# Revit family: IVLB_L4U_GM_Track 3Phase - NORDIC XTS
name_source: partatom
category: Lighting Fixtures
units: mm (PartAtom-declared; Revit-internal decimal feet)

## family parameters
Always vertical = No
Cut with Voids When Loaded = No
Light Source = No
Part Type = Normal
Room Calculation Point = No
Round Connector Dimension = Use Diameter
Shared = No
Work Plane-Based = No

## types (4) — shared parameters
Apparent Load = 0 VA
Assembly Code = 63.00
IfcExportAs = IfcLightFixtureType
IfcExportType = POINTSOURCE
Manufacturer = Light4u
URL = www.ivlibrary.com
⌂ Powered by IVLibrary = www.ivlibrary.com

## per-type parameters (varying)
| type | Length |
| NORDIC XTS 4100 | 4100 mm  [stored 13.4514 ft] |
| NORDIC XTS 4200 | 4200 mm |
| NORDIC XTS 4300 | 4300 mm |
| NORDIC XTS 4400 | 4400 mm |

note: column(s) folded — value = type name in every type: Description, Model

note: [stored X ft] marks values corroborated as IEEE doubles in the binary element streams (Revit-internal decimal feet)

## geometry (parser evidence)
native form markers: Sweep x4
no freeform markers — native parametric forms only
